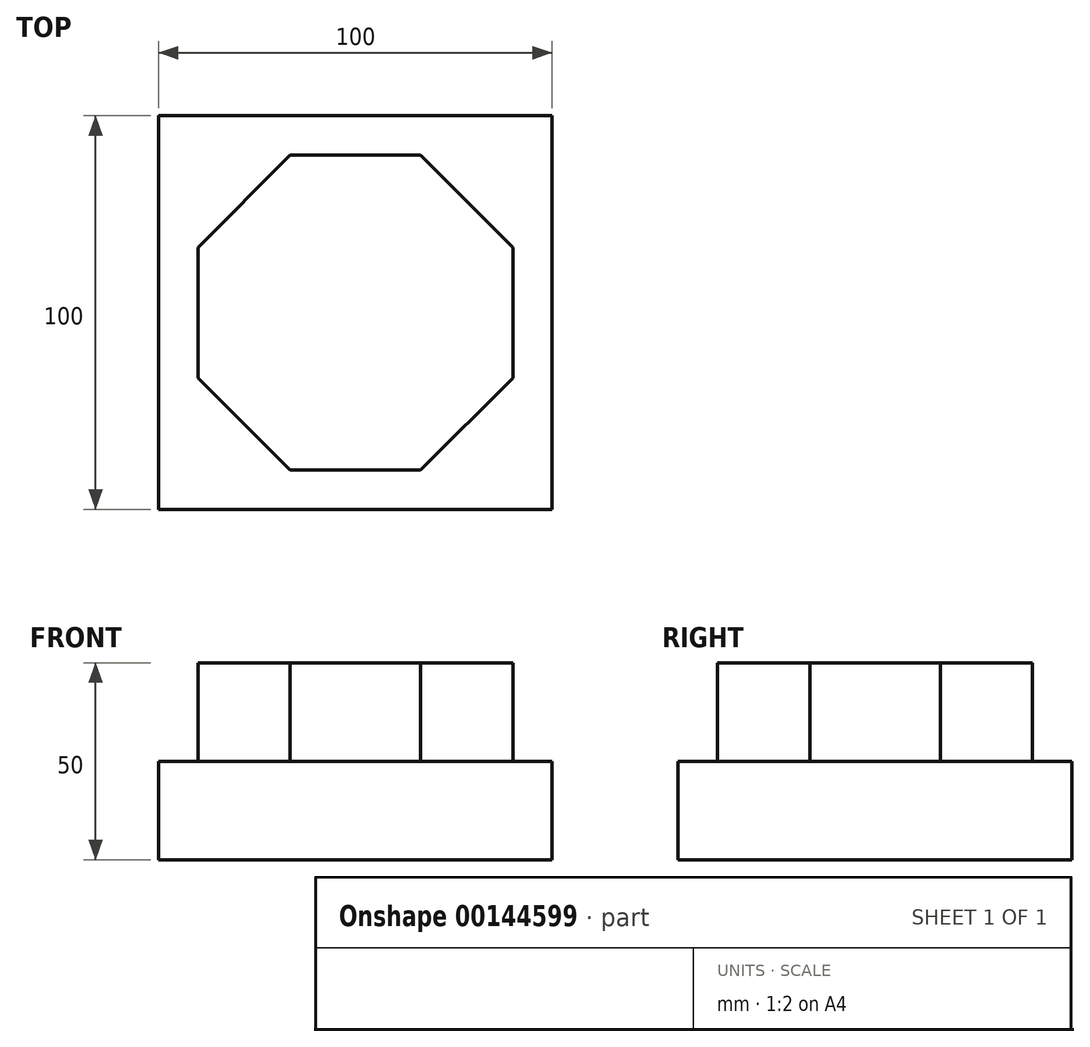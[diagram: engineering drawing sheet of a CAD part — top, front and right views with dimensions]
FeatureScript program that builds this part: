
annotation { "Feature Type Name" : "Feature", "Feature Type Description" : "" }
export const myFeature = defineFeature(function(context is Context, id is Id, definition is map)
    precondition{}
    {
        {
            var Q0;
            Q0=qCreatedBy(makeId("Top.planeOp"),FACE);
            var sketch = newSketch(context, id + "F0", { "sketchPlane" : qUnion([Q0])});
            skLineSegment(sketch, "E0.bottom", {"start": v(-50, 50) * mm, "end": v(50, 50) * mm});
            skLineSegment(sketch, "E0.top", {"start": v(-50, -50) * mm, "end": v(50, -50) * mm});
            skLineSegment(sketch, "E0.left", {"start": v(-50, 50) * mm, "end": v(-50, -50) * mm});
            skLineSegment(sketch, "E0.right", {"start": v(50, 50) * mm, "end": v(50, -50) * mm});
            skPoint(sketch, "E0.middle", {"position": v(0, 0) * mm});
            skSolve(sketch);
        }
        {
            var Q0;
            Q0 = qSketchRegion(id + "F0", true);
            extrude(context, id + "F1", {"entities" : qUnion([Q0]), "oppositeDirection" : true, "depth" : 25 * mm});
        }
        {
            var Q0;
            Q0=makeQuery(id+"F1.opExtrude","CAP_FACE",FACE,{"disambiguationData":[OSD([sQuery(id+"F0.wireOp",EDGE,"E0.bottom"),sQuery(id+"F0.wireOp",EDGE,"E0.top"),sQuery(id+"F0.wireOp",EDGE,"E0.left"),sQuery(id+"F0.wireOp",EDGE,"E0.right")])],"isStart":true});
            var sketch = newSketch(context, id + "F2", { "sketchPlane" : qUnion([Q0])});
            skCircle(sketch, "E1.cCircle", {"center": v(0, 0) * mm, "radius": 40 * mm, "construction": true});
            skLineSegment(sketch, "E1.0", {"start": v(-16.57, 40) * mm, "end": v(16.57, 40) * mm});
            skLineSegment(sketch, "E1.1", {"start": v(16.57, 40) * mm, "end": v(40, 16.57) * mm});
            skLineSegment(sketch, "E1.2", {"start": v(40, 16.57) * mm, "end": v(40, -16.57) * mm});
            skLineSegment(sketch, "E1.3", {"start": v(40, -16.57) * mm, "end": v(16.57, -40) * mm});
            skLineSegment(sketch, "E1.4", {"start": v(16.57, -40) * mm, "end": v(-16.57, -40) * mm});
            skLineSegment(sketch, "E1.5", {"start": v(-16.57, -40) * mm, "end": v(-40, -16.57) * mm});
            skLineSegment(sketch, "E1.6", {"start": v(-40, -16.57) * mm, "end": v(-40, 16.57) * mm});
            skLineSegment(sketch, "E1.7", {"start": v(-40, 16.57) * mm, "end": v(-16.57, 40) * mm});
            skPoint(sketch, "E1.0.midPoint", {"position": v(0, 40) * mm});
            skSolve(sketch);
        }
        {
            var Q0;
            Q0 = qSketchRegion(id + "F2", true);
            extrude(context, id + "F3", {"entities" : qUnion([Q0]), "operationType" : NewBodyOperationType.ADD, "depth" : 25 * mm});
        }
    });
